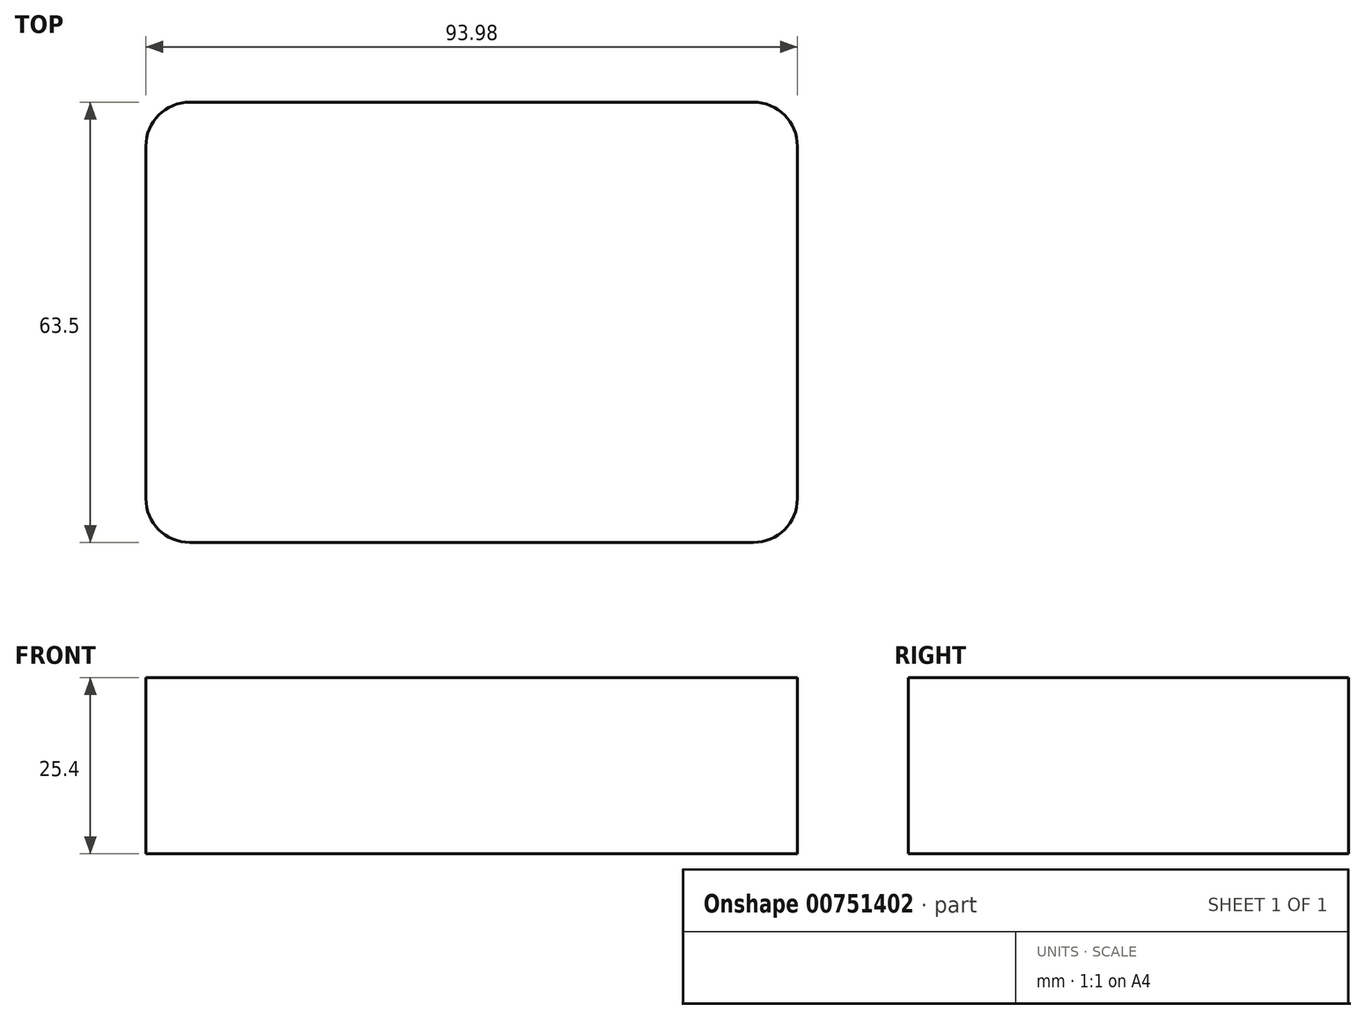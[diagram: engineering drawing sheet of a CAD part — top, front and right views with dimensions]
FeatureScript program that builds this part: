
annotation { "Feature Type Name" : "Feature", "Feature Type Description" : "" }
export const myFeature = defineFeature(function(context is Context, id is Id, definition is map)
    precondition{}
    {
        {
            var Q0;
            Q0=qCreatedBy(makeId("Top.planeOp"),FACE);
            var sketch = newSketch(context, id + "F0", { "sketchPlane" : qUnion([Q0])});
            skLineSegment(sketch, "E0.bottom", {"start": v(-46.99, 31.75) * mm, "end": v(47, 31.75) * mm});
            skLineSegment(sketch, "E0.top", {"start": v(-47, -31.75) * mm, "end": v(46.99, -31.75) * mm});
            skLineSegment(sketch, "E0.left", {"start": v(-46.99, 31.75) * mm, "end": v(-47, -31.75) * mm});
            skLineSegment(sketch, "E0.right", {"start": v(47, 31.75) * mm, "end": v(46.99, -31.75) * mm});
            skLineSegment(sketch, "E1", {"start": v(47, 31.75) * mm, "end": v(-47, -31.75) * mm, "construction": true});
            skLineSegment(sketch, "E2", {"start": v(-47, 31.75) * mm, "end": v(47, -31.75) * mm, "construction": true});
            skPoint(sketch, "E3", {"position": v(0, 0) * mm});
            skSolve(sketch);
        }
        {
            var Q0;
            Q0=makeQuery(id+"F0.imprint","IMPRINT",FACE,{"disambiguationData":[TD([[makeQuery(id+"F0.imprint","IMPRINT",EDGE,{"derivedFrom":sQuery(id+"F0.wireOp",EDGE,"E0.bottom")}),-1.0]])]});
            extrude(context, id + "F1", {"entities" : qUnion([Q0]), "depth" : 25.4 * mm, "offsetDistance" : 25.4 * mm});
        }
        {
            var Q0;
            Q0=makeQuery(id+"F1.opExtrude","SWEPT_EDGE",EDGE,{"disambiguationData":[OSD([sQuery(id+"F0.wireOp",EDGE,"E0.top"),sQuery(id+"F0.wireOp",EDGE,"E0.left")])]});
            var Q1;
            Q1=makeQuery(id+"F1.opExtrude","SWEPT_EDGE",EDGE,{"disambiguationData":[OSD([sQuery(id+"F0.wireOp",EDGE,"E0.top"),sQuery(id+"F0.wireOp",EDGE,"E0.right")])]});
            var Q2;
            Q2=makeQuery(id+"F1.opExtrude","SWEPT_EDGE",EDGE,{"disambiguationData":[OSD([sQuery(id+"F0.wireOp",EDGE,"E0.bottom"),sQuery(id+"F0.wireOp",EDGE,"E0.right")])]});
            var Q3;
            Q3=makeQuery(id+"F1.opExtrude","SWEPT_EDGE",EDGE,{"disambiguationData":[OSD([sQuery(id+"F0.wireOp",EDGE,"E0.bottom"),sQuery(id+"F0.wireOp",EDGE,"E0.left")])]});
            fillet(context, id + "F2", {"entities" : qUnion([Q0, Q1, Q2, Q3]), "radius" : 6.35 * mm, "tangentPropagation" : true, "allowEdgeOverflow" : false});
        }
    });
